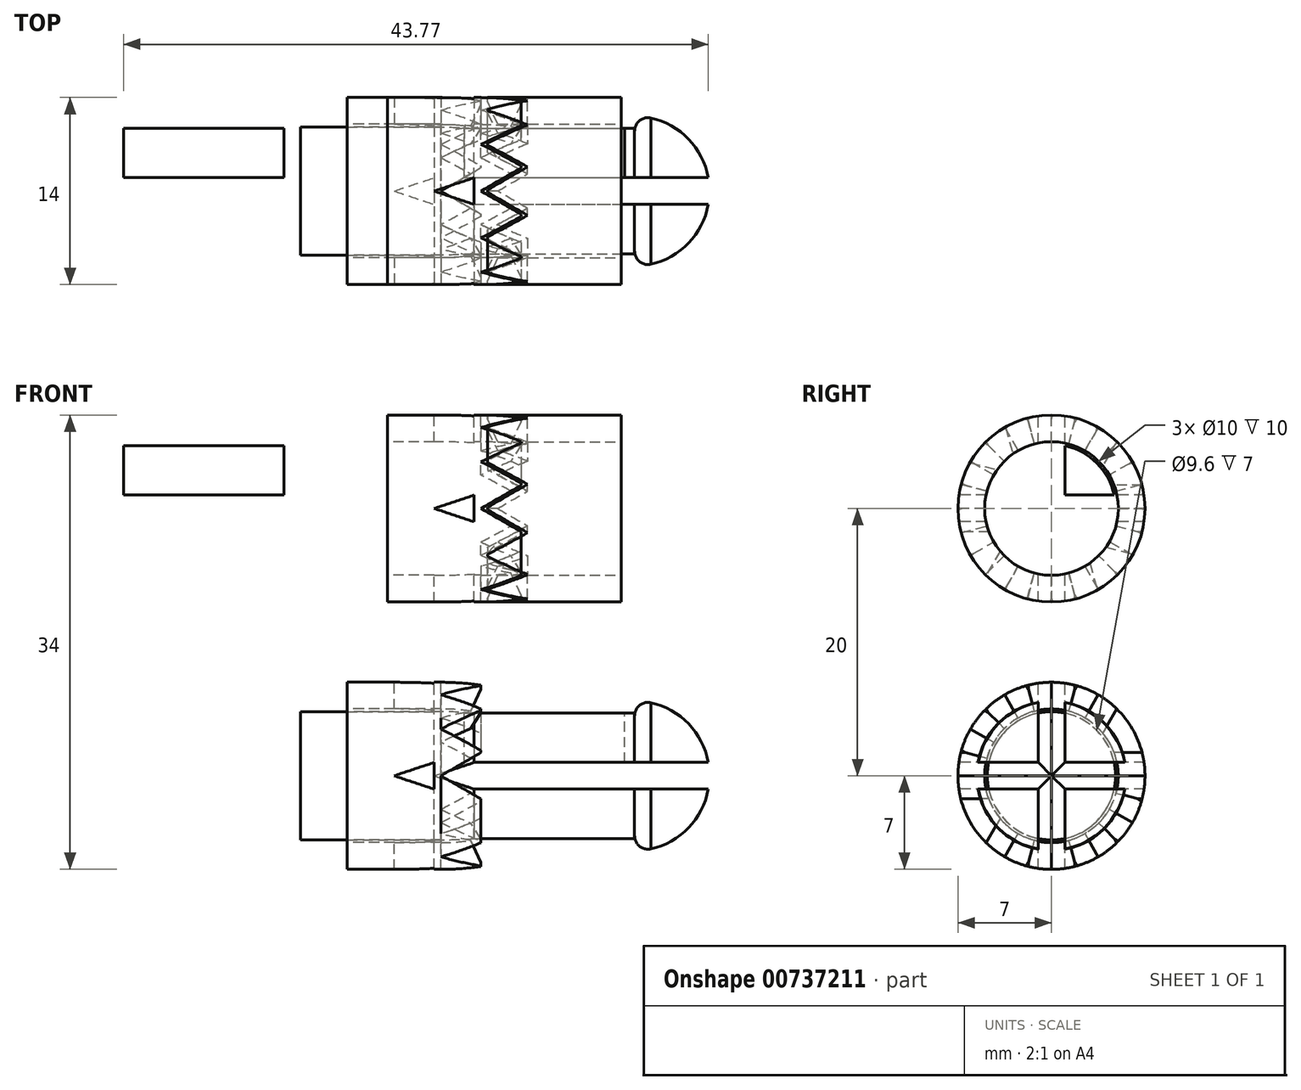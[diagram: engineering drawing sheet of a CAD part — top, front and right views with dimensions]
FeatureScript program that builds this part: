
annotation { "Feature Type Name" : "Feature", "Feature Type Description" : "" }
export const myFeature = defineFeature(function(context is Context, id is Id, definition is map)
    precondition{}
    {
        {
            var Q0;
            Q0=qCreatedBy(makeId("Right.planeOp"),FACE);
            var sketch = newSketch(context, id + "F0", { "sketchPlane" : qUnion([Q0])});
            skCircle(sketch, "E0", {"center": v(0, 0) * mm, "radius": 5 * mm});
            skCircle(sketch, "E1", {"center": v(0, 0) * mm, "radius": 7 * mm});
            skSolve(sketch);
        }
        {
            var Q0;
            Q0=makeQuery(id+"F0.imprint","IMPRINT",FACE,{"disambiguationData":[TD([[makeQuery(id+"F0.imprint","IMPRINT",EDGE,{"derivedFrom":sQuery(id+"F0.wireOp",EDGE,"E0")}),-1.0]])]});
            extrude(context, id + "F1", {"entities" : qUnion([Q0]), "oppositeDirection" : true, "depth" : 10 * mm, "offsetDistance" : 25 * mm});
        }
        {
            var Q0;
            Q0=makeQuery(id+"F1.opExtrude","CAP_FACE",FACE,{"disambiguationData":[OSD([sQuery(id+"F0.wireOp",EDGE,"E0"),sQuery(id+"F0.wireOp",EDGE,"E1")])],"isStart":false});
            var sketch = newSketch(context, id + "F2", { "sketchPlane" : qUnion([Q0])});
            skCircle(sketch, "E2.0", {"center": v(0, 0) * mm, "radius": 7 * mm});
            skCircle(sketch, "E3.cCircle", {"center": v(0, 0) * mm, "radius": 7 * mm, "construction": true});
            skLineSegment(sketch, "E3.0", {"start": v(-1.88, 7) * mm, "end": v(1.88, 7) * mm, "construction": true});
            skLineSegment(sketch, "E3.1", {"start": v(1.88, 7) * mm, "end": v(5.12, 5.12) * mm, "construction": true});
            skLineSegment(sketch, "E3.2", {"start": v(5.12, 5.12) * mm, "end": v(7, 1.88) * mm, "construction": true});
            skLineSegment(sketch, "E3.3", {"start": v(7, 1.88) * mm, "end": v(7, -1.88) * mm, "construction": true});
            skLineSegment(sketch, "E3.4", {"start": v(7, -1.88) * mm, "end": v(5.12, -5.12) * mm, "construction": true});
            skLineSegment(sketch, "E3.5", {"start": v(5.12, -5.12) * mm, "end": v(1.88, -7) * mm, "construction": true});
            skLineSegment(sketch, "E3.6", {"start": v(1.88, -7) * mm, "end": v(-1.88, -7) * mm, "construction": true});
            skLineSegment(sketch, "E3.7", {"start": v(-1.88, -7) * mm, "end": v(-5.12, -5.12) * mm, "construction": true});
            skLineSegment(sketch, "E3.8", {"start": v(-5.12, -5.12) * mm, "end": v(-7, -1.88) * mm, "construction": true});
            skLineSegment(sketch, "E3.9", {"start": v(-7, -1.88) * mm, "end": v(-7, 1.88) * mm, "construction": true});
            skLineSegment(sketch, "E3.10", {"start": v(-7, 1.88) * mm, "end": v(-5.12, 5.12) * mm, "construction": true});
            skLineSegment(sketch, "E3.11", {"start": v(-5.12, 5.12) * mm, "end": v(-1.88, 7) * mm, "construction": true});
            skPoint(sketch, "E3.0.midPoint", {"position": v(0, 7) * mm});
            skSolve(sketch);
        }
        {
            var Q0;
            Q0=sQuery(id+"F2.wireOp",EDGE,"E2.0");
            var Q1;
            Q1=sQuery(id+"F2.wireOp",VERTEX,"E3.3.start");
            cPlane(context, id + "F3", {"entities" : qUnion([Q0, Q1]), "cplaneType" : CPlaneType.CURVE_POINT, "offset" : 25 * mm, "width" : 150 * mm, "height" : 150 * mm});
        }
        {
            var Q0;
            Q0=qCreatedBy(id+"F3.planeOp",FACE);
            var sketch = newSketch(context, id + "F4", { "sketchPlane" : qUnion([Q0])});
            skLineSegment(sketch, "E4.0", {"start": v(-10, -7) * mm, "end": v(-10, 7) * mm});
            skLineSegment(sketch, "E4.1", {"start": v(0, 7) * mm, "end": v(0, -7) * mm});
            skLineSegment(sketch, "E5", {"start": v(0, 7) * mm, "end": v(-10, 7) * mm});
            skLineSegment(sketch, "E6", {"start": v(0, -7) * mm, "end": v(-10, -7) * mm});
            skLineSegment(sketch, "E7", {"start": v(-7, 7) * mm, "end": v(-7, -7) * mm});
            skPoint(sketch, "E8", {"position": v(-7, 0) * mm});
            skLineSegment(sketch, "E9", {"start": v(-7, 0) * mm, "end": v(-10, 1.73) * mm});
            skLineSegment(sketch, "E10", {"start": v(-7, 0) * mm, "end": v(-10, -1.73) * mm});
            skSolve(sketch);
        }
        {
            var Q0;
            Q0=sQuery(id+"F2.wireOp",EDGE,"E2.0");
            var Q1;
            Q1=sQuery(id+"F2.wireOp",VERTEX,"E3.2.start");
            cPlane(context, id + "F5", {"entities" : qUnion([Q0, Q1]), "cplaneType" : CPlaneType.CURVE_POINT, "offset" : 25 * mm, "width" : 150 * mm, "height" : 150 * mm});
        }
        {
            var Q0;
            Q0=qCreatedBy(id+"F5.planeOp",FACE);
            var sketch = newSketch(context, id + "F6", { "sketchPlane" : qUnion([Q0])});
            skLineSegment(sketch, "E11.0", {"start": v(10, 7) * mm, "end": v(10, -7) * mm});
            skLineSegment(sketch, "E12.0", {"start": v(0, -7) * mm, "end": v(0, 7) * mm});
            skLineSegment(sketch, "E13", {"start": v(0, -7) * mm, "end": v(10, -7) * mm});
            skLineSegment(sketch, "E14", {"start": v(0, 7) * mm, "end": v(10, 7) * mm});
            skLineSegment(sketch, "E15.0", {"start": v(7, -6.06) * mm, "end": v(7, 6.06) * mm});
            skLineSegment(sketch, "E16", {"start": v(7, 0) * mm, "end": v(10, -1.73) * mm});
            skLineSegment(sketch, "E17", {"start": v(7, 0) * mm, "end": v(10, 1.73) * mm});
            skSolve(sketch);
        }
        {
            var Q0;
            Q0=sQuery(id+"F2.wireOp",EDGE,"E2.0");
            var Q1;
            Q1=sQuery(id+"F2.wireOp",VERTEX,"E3.1.start");
            cPlane(context, id + "F7", {"entities" : qUnion([Q0, Q1]), "cplaneType" : CPlaneType.CURVE_POINT, "offset" : 25 * mm, "width" : 150 * mm, "height" : 150 * mm});
        }
        {
            var Q0;
            Q0=qCreatedBy(id+"F7.planeOp",FACE);
            var sketch = newSketch(context, id + "F8", { "sketchPlane" : qUnion([Q0])});
            skLineSegment(sketch, "E18.0", {"start": v(10, 7) * mm, "end": v(10, -7) * mm});
            skLineSegment(sketch, "E18.1", {"start": v(0, -7) * mm, "end": v(0, 7) * mm});
            skLineSegment(sketch, "E19", {"start": v(0, -7) * mm, "end": v(10, -7) * mm});
            skLineSegment(sketch, "E20", {"start": v(0, 7) * mm, "end": v(10, 7) * mm});
            skLineSegment(sketch, "E21.0", {"start": v(7, -5.25) * mm, "end": v(7, 5.25) * mm});
            skPoint(sketch, "E22", {"position": v(7, 0) * mm});
            skLineSegment(sketch, "E23", {"start": v(7, 0) * mm, "end": v(10, -1.73) * mm});
            skLineSegment(sketch, "E24", {"start": v(7, 0) * mm, "end": v(10, 1.73) * mm});
            skSolve(sketch);
        }
        {
            var Q0;
            Q0=sQuery(id+"F2.wireOp",EDGE,"E2.0");
            var Q1;
            Q1=sQuery(id+"F2.wireOp",VERTEX,"E3.11.end");
            cPlane(context, id + "F9", {"entities" : qUnion([Q0, Q1]), "cplaneType" : CPlaneType.CURVE_POINT, "offset" : 25 * mm, "width" : 150 * mm, "height" : 150 * mm});
        }
        {
            var Q0;
            Q0=qCreatedBy(id+"F9.planeOp",FACE);
            var sketch = newSketch(context, id + "F10", { "sketchPlane" : qUnion([Q0])});
            skLineSegment(sketch, "E25.0", {"start": v(10, 7) * mm, "end": v(10, -7) * mm});
            skLineSegment(sketch, "E25.1", {"start": v(0, -7) * mm, "end": v(0, 7) * mm});
            skLineSegment(sketch, "E26", {"start": v(0, -7) * mm, "end": v(10, -7) * mm});
            skLineSegment(sketch, "E27", {"start": v(0, 7) * mm, "end": v(10, 7) * mm});
            skLineSegment(sketch, "E28.0", {"start": v(7, -4.55) * mm, "end": v(7, 4.55) * mm});
            skPoint(sketch, "E29", {"position": v(7, 0) * mm});
            skLineSegment(sketch, "E30", {"start": v(7, 0) * mm, "end": v(10, 1.73) * mm});
            skLineSegment(sketch, "E31", {"start": v(7, 0) * mm, "end": v(10, -1.73) * mm});
            skSolve(sketch);
        }
        {
            var Q0;
            Q0=sQuery(id+"F2.wireOp",EDGE,"E2.0");
            var Q1;
            Q1=sQuery(id+"F2.wireOp",VERTEX,"E3.10.end");
            cPlane(context, id + "F11", {"entities" : qUnion([Q0, Q1]), "cplaneType" : CPlaneType.CURVE_POINT, "offset" : 25 * mm, "width" : 150 * mm, "height" : 150 * mm});
        }
        {
            var Q0;
            Q0=qCreatedBy(id+"F11.planeOp",FACE);
            var sketch = newSketch(context, id + "F12", { "sketchPlane" : qUnion([Q0])});
            skLineSegment(sketch, "E32.0", {"start": v(-10, -7) * mm, "end": v(-10, 7) * mm});
            skLineSegment(sketch, "E32.1", {"start": v(0, 7) * mm, "end": v(0, -7) * mm});
            skLineSegment(sketch, "E33", {"start": v(0, 7) * mm, "end": v(-10, 7) * mm});
            skLineSegment(sketch, "E34", {"start": v(0, -7) * mm, "end": v(-10, -7) * mm});
            skLineSegment(sketch, "E35.0", {"start": v(-7, 3.94) * mm, "end": v(-7, -3.94) * mm});
            skLineSegment(sketch, "E36", {"start": v(-7, 0) * mm, "end": v(-10, -1.73) * mm});
            skLineSegment(sketch, "E37", {"start": v(-7, 0) * mm, "end": v(-10, 1.73) * mm});
            skSolve(sketch);
        }
        {
            var Q0;
            Q0=sQuery(id+"F2.wireOp",EDGE,"E2.0");
            var Q1;
            Q1=sQuery(id+"F2.wireOp",VERTEX,"E3.9.end");
            cPlane(context, id + "F13", {"entities" : qUnion([Q0, Q1]), "cplaneType" : CPlaneType.CURVE_POINT, "offset" : 25 * mm, "width" : 150 * mm, "height" : 150 * mm});
        }
        {
            var Q0;
            Q0=qCreatedBy(id+"F13.planeOp",FACE);
            var sketch = newSketch(context, id + "F14", { "sketchPlane" : qUnion([Q0])});
            skLineSegment(sketch, "E38.0", {"start": v(-10, -7) * mm, "end": v(-10, 7) * mm});
            skLineSegment(sketch, "E38.1", {"start": v(0, 7) * mm, "end": v(0, -7) * mm});
            skLineSegment(sketch, "E39.0", {"start": v(-7, 3.4) * mm, "end": v(-7, -3.4) * mm});
            skLineSegment(sketch, "E40", {"start": v(-7, 0) * mm, "end": v(-10, 1.73) * mm});
            skLineSegment(sketch, "E41", {"start": v(-7, 0) * mm, "end": v(-10, -1.73) * mm});
            skSolve(sketch);
        }
        {
            var Q0;
            {var subQ0=sQuery(id+"F4.wireOp",EDGE,"E9");Q0=makeQuery(id+"F4.imprint","IMPRINT",FACE,{"disambiguationData":[TD([[makeQuery(id+"F4.imprint","IMPRINT",EDGE,{"derivedFrom":subQ0}),1.0]])]});}
            extrude(context, id + "F15", {"entities" : qUnion([Q0]), "operationType" : NewBodyOperationType.REMOVE, "endBound" : BoundingType.SYMMETRIC, "oppositeDirection" : true, "depth" : 14.5 * mm, "offsetDistance" : 25 * mm});
        }
        {
            var Q0;
            {var subQ0=sQuery(id+"F6.wireOp",EDGE,"E16");Q0=makeQuery(id+"F6.imprint","IMPRINT",FACE,{"disambiguationData":[TD([[makeQuery(id+"F6.imprint","IMPRINT",EDGE,{"derivedFrom":subQ0}),1.0]])]});}
            extrude(context, id + "F16", {"entities" : qUnion([Q0]), "operationType" : NewBodyOperationType.REMOVE, "endBound" : BoundingType.SYMMETRIC, "depth" : 14.5 * mm, "offsetDistance" : 25 * mm});
        }
        {
            var Q0;
            {var subQ0=sQuery(id+"F8.wireOp",EDGE,"E23");Q0=makeQuery(id+"F8.imprint","IMPRINT",FACE,{"disambiguationData":[TD([[makeQuery(id+"F8.imprint","IMPRINT",EDGE,{"derivedFrom":subQ0}),1.0]])]});}
            extrude(context, id + "F17", {"entities" : qUnion([Q0]), "operationType" : NewBodyOperationType.REMOVE, "endBound" : BoundingType.SYMMETRIC, "oppositeDirection" : true, "depth" : 14.5 * mm, "offsetDistance" : 25 * mm});
        }
        {
            var Q0;
            {var subQ0=sQuery(id+"F10.wireOp",EDGE,"E30");Q0=makeQuery(id+"F10.imprint","IMPRINT",FACE,{"disambiguationData":[TD([[makeQuery(id+"F10.imprint","IMPRINT",EDGE,{"derivedFrom":subQ0}),-1.0]])]});}
            extrude(context, id + "F18", {"entities" : qUnion([Q0]), "operationType" : NewBodyOperationType.REMOVE, "endBound" : BoundingType.SYMMETRIC, "oppositeDirection" : true, "depth" : 14.5 * mm, "offsetDistance" : 25 * mm});
        }
        {
            var Q0;
            {var subQ0=sQuery(id+"F14.wireOp",EDGE,"E40");Q0=makeQuery(id+"F14.imprint","IMPRINT",FACE,{"disambiguationData":[TD([[makeQuery(id+"F14.imprint","IMPRINT",EDGE,{"derivedFrom":subQ0}),1.0]])]});}
            extrude(context, id + "F19", {"entities" : qUnion([Q0]), "operationType" : NewBodyOperationType.REMOVE, "endBound" : BoundingType.SYMMETRIC, "oppositeDirection" : true, "depth" : 14.5 * mm, "offsetDistance" : 25 * mm});
        }
        {
            var Q0;
            {var subQ0=sQuery(id+"F12.wireOp",EDGE,"E36");Q0=makeQuery(id+"F12.imprint","IMPRINT",FACE,{"disambiguationData":[TD([[makeQuery(id+"F12.imprint","IMPRINT",EDGE,{"derivedFrom":subQ0}),-1.0]])]});}
            extrude(context, id + "F20", {"entities" : qUnion([Q0]), "operationType" : NewBodyOperationType.REMOVE, "endBound" : BoundingType.SYMMETRIC, "oppositeDirection" : true, "depth" : 14.5 * mm, "offsetDistance" : 25 * mm});
        }
        {
            var Q0;
            Q0=makeQuery(id+"F1.opExtrude","CAP_FACE",FACE,{"disambiguationData":[OSD([sQuery(id+"F0.wireOp",EDGE,"E0"),sQuery(id+"F0.wireOp",EDGE,"E1")])],"isStart":true});
            var sketch = newSketch(context, id + "F21", { "sketchPlane" : qUnion([Q0])});
            skCircle(sketch, "E42.0", {"center": v(0, 0) * mm, "radius": 7 * mm});
            skLineSegment(sketch, "E43", {"start": v(0, 7) * mm, "end": v(0, -7) * mm, "construction": true});
            skLineSegment(sketch, "E44", {"start": v(-7, 0) * mm, "end": v(7, 0) * mm, "construction": true});
            skSolve(sketch);
        }
        {
            var Q0;
            Q0=makeQuery(id+"F1.opExtrude","SWEPT_BODY",BODY,{"disambiguationData":[OSD([sQuery(id+"F0.wireOp",EDGE,"E0"),sQuery(id+"F0.wireOp",EDGE,"E1")])]});
            var Q1;
            Q1=sQuery(id+"F21.wireOp",EDGE,"E43");
            transform(context, id + "F22", {"entities" : qUnion([Q0]), "transformType" : TransformType.ROTATION, "transformAxis" : qUnion([Q1]), "angle" : 180 * degree, "makeCopy" : true});
        }
        {
            var Q0;
            Q0=makeQuery(id+"F22.opPattern","COPY",BODY,{"derivedFrom":makeQuery(id+"F1.opExtrude","SWEPT_BODY",BODY,{"disambiguationData":[OSD([sQuery(id+"F0.wireOp",EDGE,"E0"),sQuery(id+"F0.wireOp",EDGE,"E1")])]}),"instanceName":"1"});
            transform(context, id + "F23", {"entities" : qUnion([Q0]), "transformType" : TransformType.TRANSLATION_3D, "dx" : -17.5 * mm, "dy" : 0 * mm, "dz" : 0 * mm, "makeCopy" : false});
        }
        {
            var Q0;
            Q0=makeQuery(id+"F22.opPattern","COPY",BODY,{"derivedFrom":makeQuery(id+"F1.opExtrude","SWEPT_BODY",BODY,{"disambiguationData":[OSD([sQuery(id+"F0.wireOp",EDGE,"E0"),sQuery(id+"F0.wireOp",EDGE,"E1")])]}),"instanceName":"1"});
            var Q1;
            Q1=makeQuery(id+"F22.opPattern","COPY",EDGE,{"derivedFrom":makeQuery(id+"F1.opExtrude","CAP_EDGE",EDGE,{"disambiguationData":[OSD([sQuery(id+"F0.wireOp",EDGE,"E0")])],"isStart":true}),"instanceName":"1"});
            transform(context, id + "F24", {"entities" : qUnion([Q0]), "transformType" : TransformType.ROTATION, "transformAxis" : qUnion([Q1]), "angle" : 15 * degree, "makeCopy" : false});
        }
        {
            var Q0;
            Q0=makeQuery(id+"F1.opExtrude","CAP_FACE",FACE,{"disambiguationData":[OSD([sQuery(id+"F0.wireOp",EDGE,"E0"),sQuery(id+"F0.wireOp",EDGE,"E1")])],"isStart":true});
            cPlane(context, id + "F25", {"entities" : qUnion([Q0]), "cplaneType" : CPlaneType.OFFSET, "offset" : 1 * mm, "width" : 150 * mm, "height" : 150 * mm});
        }
        {
            var Q0;
            Q0=qCreatedBy(id+"F25.planeOp",FACE);
            var sketch = newSketch(context, id + "F26", { "sketchPlane" : qUnion([Q0])});
            skCircle(sketch, "E45", {"center": v(0, 0) * mm, "radius": 4.8 * mm});
            skLineSegment(sketch, "E46", {"start": v(0, 0) * mm, "end": v(4.8, 0) * mm});
            skLineSegment(sketch, "E47", {"start": v(0, 0) * mm, "end": v(-4.8, 0) * mm});
            skLineSegment(sketch, "E48", {"start": v(0, 0) * mm, "end": v(0, -4.8) * mm});
            skLineSegment(sketch, "E49", {"start": v(0, 0) * mm, "end": v(0, 4.8) * mm});
            skLineSegment(sketch, "E50.0", {"start": v(1, -1) * mm, "end": v(4.7, -1) * mm});
            skLineSegment(sketch, "E50.1", {"start": v(1, -1) * mm, "end": v(1, -4.7) * mm});
            skLineSegment(sketch, "E51.MirrorCS", {"start": v(1, 1) * mm, "end": v(4.7, 1) * mm});
            skLineSegment(sketch, "E52.MirrorCS", {"start": v(1, 1) * mm, "end": v(1, 4.7) * mm});
            skLineSegment(sketch, "E53.MirrorCS", {"start": v(-1, -1) * mm, "end": v(-1, -4.7) * mm});
            skLineSegment(sketch, "E54.MirrorCS", {"start": v(-1, -1) * mm, "end": v(-4.7, -1) * mm});
            skLineSegment(sketch, "E55.MirrorCS", {"start": v(-1, 1) * mm, "end": v(-4.7, 1) * mm});
            skLineSegment(sketch, "E56.MirrorCS", {"start": v(-1, 1) * mm, "end": v(-1, 4.7) * mm});
            skSolve(sketch);
        }
        {
            var Q0;
            {var subQ0=sQuery(id+"F26.wireOp",EDGE,"E51.MirrorCS");Q0=makeQuery(id+"F26.imprint","IMPRINT",FACE,{"disambiguationData":[TD([[makeQuery(id+"F26.imprint","IMPRINT",EDGE,{"derivedFrom":subQ0}),1.0]])]});}
            var Q1;
            {var subQ0=sQuery(id+"F26.wireOp",EDGE,"E50.0");Q1=makeQuery(id+"F26.imprint","IMPRINT",FACE,{"disambiguationData":[TD([[makeQuery(id+"F26.imprint","IMPRINT",EDGE,{"derivedFrom":subQ0}),-1.0]])]});}
            var Q2;
            {var subQ0=sQuery(id+"F26.wireOp",EDGE,"E53.MirrorCS");Q2=makeQuery(id+"F26.imprint","IMPRINT",FACE,{"disambiguationData":[TD([[makeQuery(id+"F26.imprint","IMPRINT",EDGE,{"derivedFrom":subQ0}),-1.0]])]});}
            var Q3;
            {var subQ0=sQuery(id+"F26.wireOp",EDGE,"E55.MirrorCS");Q3=makeQuery(id+"F26.imprint","IMPRINT",FACE,{"disambiguationData":[TD([[makeQuery(id+"F26.imprint","IMPRINT",EDGE,{"derivedFrom":subQ0}),-1.0]])]});}
            extrude(context, id + "F27", {"entities" : qUnion([Q0, Q1, Q2, Q3]), "oppositeDirection" : true, "depth" : 12 * mm, "offsetDistance" : 25 * mm});
        }
        {
            var Q0;
            Q0=makeQuery(id+"F27.opExtrude","CAP_FACE",FACE,{"disambiguationData":[OSD([sQuery(id+"F26.wireOp",EDGE,"E45"),sQuery(id+"F26.wireOp",EDGE,"E51.MirrorCS"),sQuery(id+"F26.wireOp",EDGE,"E52.MirrorCS")])],"isStart":false});
            var sketch = newSketch(context, id + "F28", { "sketchPlane" : qUnion([Q0])});
            skPoint(sketch, "E57.0", {"position": v(0, 0) * mm});
            skLineSegment(sketch, "E58.0", {"start": v(1, 1) * mm, "end": v(1, 4.7) * mm});
            skLineSegment(sketch, "E58.1", {"start": v(1, 1) * mm, "end": v(4.7, 1) * mm});
            skArc(sketch, "E58.2", {"start": v(1, 4.7) * mm, "mid": v(3.4, 3.4) * mm, "end": v(4.7, 1) * mm});
            skLineSegment(sketch, "E58.3", {"start": v(-1, 1) * mm, "end": v(-1, 4.7) * mm});
            skArc(sketch, "E58.4", {"start": v(-4.7, 1) * mm, "mid": v(-3.4, 3.4) * mm, "end": v(-1, 4.7) * mm});
            skLineSegment(sketch, "E58.5", {"start": v(-1, 1) * mm, "end": v(-4.7, 1) * mm});
            skLineSegment(sketch, "E58.6", {"start": v(-1, -1) * mm, "end": v(-4.7, -1) * mm});
            skLineSegment(sketch, "E58.7", {"start": v(-1, -1) * mm, "end": v(-1, -4.7) * mm});
            skLineSegment(sketch, "E58.8", {"start": v(1, -1) * mm, "end": v(1, -4.7) * mm});
            skLineSegment(sketch, "E58.9", {"start": v(1, -1) * mm, "end": v(4.7, -1) * mm});
            skArc(sketch, "E58.10", {"start": v(4.7, -1) * mm, "mid": v(3.4, -3.4) * mm, "end": v(1, -4.7) * mm});
            skArc(sketch, "E58.11", {"start": v(-1, -4.7) * mm, "mid": v(-3.4, -3.4) * mm, "end": v(-4.7, -1) * mm});
            skCircle(sketch, "E59", {"center": v(0, 0) * mm, "radius": 4.8 * mm});
            skSolve(sketch);
        }
        {
            var Q0;
            {var subQ2=sQuery(id+"F28.wireOp",EDGE,"E58.0");Q0=makeQuery(id+"F28.imprint","IMPRINT",FACE,{"disambiguationData":[TD([[makeQuery(id+"F28.imprint","IMPRINT",EDGE,{"derivedFrom":subQ2}),1.0]])]});}
            var Q1;
            {var subQ0=sQuery(id+"F28.wireOp",EDGE,"E58.3");Q1=makeQuery(id+"F28.imprint","IMPRINT",FACE,{"disambiguationData":[TD([[makeQuery(id+"F28.imprint","IMPRINT",EDGE,{"derivedFrom":subQ0}),1.0]])]});}
            var Q2;
            {var subQ0=sQuery(id+"F28.wireOp",EDGE,"E58.6");Q2=makeQuery(id+"F28.imprint","IMPRINT",FACE,{"disambiguationData":[TD([[makeQuery(id+"F28.imprint","IMPRINT",EDGE,{"derivedFrom":subQ0}),1.0]])]});}
            var Q3;
            {var subQ0=sQuery(id+"F28.wireOp",EDGE,"E58.0");Q3=makeQuery(id+"F28.imprint","IMPRINT",FACE,{"disambiguationData":[TD([[makeQuery(id+"F28.imprint","IMPRINT",EDGE,{"derivedFrom":subQ0}),-1.0]])]});}
            var Q4;
            {var subQ0=sQuery(id+"F28.wireOp",EDGE,"E58.8");Q4=makeQuery(id+"F28.imprint","IMPRINT",FACE,{"disambiguationData":[TD([[makeQuery(id+"F28.imprint","IMPRINT",EDGE,{"derivedFrom":subQ0}),1.0]])]});}
            extrude(context, id + "F29", {"entities" : qUnion([Q0, Q1, Q2, Q3, Q4]), "depth" : 15 * mm, "offsetDistance" : 25 * mm});
        }
        {
            var Q0;
            Q0=qCreatedBy(makeId("Front.planeOp"),FACE);
            var sketch = newSketch(context, id + "F30", { "sketchPlane" : qUnion([Q0])});
            skLineSegment(sketch, "E60.0", {"start": v(-11, -4.8) * mm, "end": v(-11, 4.8) * mm});
            skLineSegment(sketch, "E61", {"start": v(-11, 4.8) * mm, "end": v(-14, 4.8) * mm});
            skLineSegment(sketch, "E62", {"start": v(-14, 4.8) * mm, "end": v(-14, -4.8) * mm});
            skLineSegment(sketch, "E63", {"start": v(-14, -4.8) * mm, "end": v(-11, -4.8) * mm});
            skPoint(sketch, "E64", {"position": v(-14, 0) * mm});
            skLineSegment(sketch, "E65.0", {"start": v(-11, 1) * mm, "end": v(1, 1) * mm});
            skLineSegment(sketch, "E65.1", {"start": v(-11, -1) * mm, "end": v(1, -1) * mm});
            skLineSegment(sketch, "E66", {"start": v(-14, 0) * mm, "end": v(-11, 1) * mm});
            skLineSegment(sketch, "E67", {"start": v(-14, 0) * mm, "end": v(-11, -1) * mm});
            skSolve(sketch);
        }
        {
            var Q0;
            {var subQ0=sQuery(id+"F30.wireOp",EDGE,"E66");Q0=makeQuery(id+"F30.imprint","IMPRINT",FACE,{"disambiguationData":[TD([[makeQuery(id+"F30.imprint","IMPRINT",EDGE,{"derivedFrom":subQ0}),-1.0]])]});}
            extrude(context, id + "F31", {"entities" : qUnion([Q0]), "operationType" : NewBodyOperationType.REMOVE, "endBound" : BoundingType.SYMMETRIC, "oppositeDirection" : true, "depth" : 14.5 * mm, "offsetDistance" : 25 * mm});
        }
        {
            var Q0;
            Q0=qCreatedBy(makeId("Top.planeOp"),FACE);
            var sketch = newSketch(context, id + "F32", { "sketchPlane" : qUnion([Q0])});
            skLineSegment(sketch, "E68.0", {"start": v(-11, 4.7) * mm, "end": v(-11, -4.7) * mm});
            skLineSegment(sketch, "E68.1", {"start": v(-11, -1) * mm, "end": v(1, -1) * mm});
            skLineSegment(sketch, "E68.2", {"start": v(-11, 1) * mm, "end": v(1, 1) * mm});
            skLineSegment(sketch, "E69", {"start": v(-11, -4.7) * mm, "end": v(-14, -4.7) * mm});
            skLineSegment(sketch, "E70", {"start": v(-14, -4.7) * mm, "end": v(-14, 4.7) * mm});
            skLineSegment(sketch, "E71", {"start": v(-14, 4.7) * mm, "end": v(-11, 4.7) * mm});
            skPoint(sketch, "E72", {"position": v(-14, 0) * mm});
            skLineSegment(sketch, "E73", {"start": v(-14, 0) * mm, "end": v(-11, -1) * mm});
            skLineSegment(sketch, "E74", {"start": v(-14, 0) * mm, "end": v(-11, 1) * mm});
            skSolve(sketch);
        }
        {
            var Q0;
            {var subQ0=sQuery(id+"F32.wireOp",EDGE,"E73");Q0=makeQuery(id+"F32.imprint","IMPRINT",FACE,{"disambiguationData":[TD([[makeQuery(id+"F32.imprint","IMPRINT",EDGE,{"derivedFrom":subQ0}),1.0]])]});}
            extrude(context, id + "F33", {"entities" : qUnion([Q0]), "operationType" : NewBodyOperationType.REMOVE, "endBound" : BoundingType.SYMMETRIC, "oppositeDirection" : true, "depth" : 14.5 * mm, "offsetDistance" : 25 * mm});
        }
        {
            var Q0;
            Q0=qCreatedBy(id+"F25.planeOp",FACE);
            var sketch = newSketch(context, id + "F34", { "sketchPlane" : qUnion([Q0])});
            skLineSegment(sketch, "E75.0", {"start": v(0, 0) * mm, "end": v(-4.8, 0) * mm});
            skLineSegment(sketch, "E75.1", {"start": v(4.8, 0) * mm, "end": v(0, 0) * mm});
            skLineSegment(sketch, "E75.2", {"start": v(0, 0) * mm, "end": v(0, 4.8) * mm});
            skLineSegment(sketch, "E75.3", {"start": v(0, -4.8) * mm, "end": v(0, 0) * mm});
            skLineSegment(sketch, "E76.0", {"start": v(-1, 1) * mm, "end": v(-4.7, 1) * mm});
            skLineSegment(sketch, "E76.1", {"start": v(-1, -1) * mm, "end": v(-4.7, -1) * mm});
            skLineSegment(sketch, "E76.2", {"start": v(-1, -1) * mm, "end": v(-1, -4.7) * mm});
            skLineSegment(sketch, "E76.3", {"start": v(1, -1) * mm, "end": v(1, -4.7) * mm});
            skLineSegment(sketch, "E76.4", {"start": v(1, 1) * mm, "end": v(1, 4.7) * mm});
            skLineSegment(sketch, "E76.5", {"start": v(-1, 1) * mm, "end": v(-1, 4.7) * mm});
            skLineSegment(sketch, "E76.6", {"start": v(1, -1) * mm, "end": v(4.7, -1) * mm});
            skLineSegment(sketch, "E76.7", {"start": v(1, 1) * mm, "end": v(4.7, 1) * mm});
            skLineSegment(sketch, "E77", {"start": v(-4.7, -1) * mm, "end": v(-5.7, -1) * mm});
            skLineSegment(sketch, "E78", {"start": v(-5.7, -1) * mm, "end": v(-5.7, 1) * mm});
            skLineSegment(sketch, "E79", {"start": v(-5.7, 1) * mm, "end": v(-4.7, 1) * mm});
            skLineSegment(sketch, "E80", {"start": v(-1, -4.7) * mm, "end": v(-1, -5.7) * mm});
            skLineSegment(sketch, "E81", {"start": v(-1, -5.7) * mm, "end": v(1, -5.7) * mm});
            skLineSegment(sketch, "E82", {"start": v(1, -5.7) * mm, "end": v(1, -4.7) * mm});
            skLineSegment(sketch, "E83", {"start": v(4.7, -1) * mm, "end": v(5.7, -1) * mm});
            skLineSegment(sketch, "E84", {"start": v(5.7, -1) * mm, "end": v(5.7, 1) * mm});
            skLineSegment(sketch, "E85", {"start": v(5.7, 1) * mm, "end": v(4.7, 1) * mm});
            skLineSegment(sketch, "E86", {"start": v(1, 4.7) * mm, "end": v(1, 5.7) * mm});
            skLineSegment(sketch, "E87", {"start": v(1, 5.7) * mm, "end": v(-1, 5.7) * mm});
            skLineSegment(sketch, "E88", {"start": v(-1, 5.7) * mm, "end": v(-1, 4.7) * mm});
            skCircle(sketch, "E89", {"center": v(0, 0) * mm, "radius": 5.7 * mm});
            skLineSegment(sketch, "E90", {"start": v(4.8, 0) * mm, "end": v(5.7, 0) * mm});
            skLineSegment(sketch, "E91", {"start": v(0, 4.8) * mm, "end": v(0, 5.7) * mm});
            skLineSegment(sketch, "E92", {"start": v(-4.8, 0) * mm, "end": v(-5.7, 0) * mm});
            skLineSegment(sketch, "E93", {"start": v(0, -4.8) * mm, "end": v(0, -5.7) * mm});
            skSolve(sketch);
        }
        {
            var Q0;
            {var subQ3=sQuery(id+"F34.wireOp",EDGE,"E75.0");Q0=makeQuery(id+"F34.imprint","IMPRINT",FACE,{"disambiguationData":[TD([[makeQuery(id+"F34.imprint","IMPRINT",EDGE,{"derivedFrom":subQ3}),1.0]])]});}
            var Q1;
            {var subQ3=sQuery(id+"F34.wireOp",EDGE,"E75.0");Q1=makeQuery(id+"F34.imprint","IMPRINT",FACE,{"disambiguationData":[TD([[makeQuery(id+"F34.imprint","IMPRINT",EDGE,{"derivedFrom":subQ3}),-1.0]])]});}
            var Q2;
            {var subQ0=sQuery(id+"F34.wireOp",EDGE,"E76.0");Q2=makeQuery(id+"F34.imprint","IMPRINT",FACE,{"disambiguationData":[TD([[makeQuery(id+"F34.imprint","IMPRINT",EDGE,{"derivedFrom":subQ0}),-1.0]])]});}
            var Q3;
            {var subQ0=sQuery(id+"F34.wireOp",EDGE,"E76.1");Q3=makeQuery(id+"F34.imprint","IMPRINT",FACE,{"disambiguationData":[TD([[makeQuery(id+"F34.imprint","IMPRINT",EDGE,{"derivedFrom":subQ0}),1.0]])]});}
            var Q4;
            Q4=sQuery(id+"F34.wireOp",EDGE,"E75.2");
            revolve(context, id + "F35", {"surfaceOperationType" : NewSurfaceOperationType.NEW, "entities" : qUnion([Q0, Q1, Q2, Q3]), "axis" : qUnion([Q4]), "revolveType" : RevolveType.ONE_DIRECTION, "angle" : 180 * degree});
        }
        {
            var Q0;
            {var subQ3=sQuery(id+"F34.wireOp",EDGE,"E75.0");Q0=makeQuery(id+"F34.imprint","IMPRINT",FACE,{"disambiguationData":[TD([[makeQuery(id+"F34.imprint","IMPRINT",EDGE,{"derivedFrom":subQ3}),1.0]])]});}
            var Q1;
            {var subQ3=sQuery(id+"F34.wireOp",EDGE,"E75.0");Q1=makeQuery(id+"F34.imprint","IMPRINT",FACE,{"disambiguationData":[TD([[makeQuery(id+"F34.imprint","IMPRINT",EDGE,{"derivedFrom":subQ3}),-1.0]])]});}
            var Q2;
            {var subQ0=sQuery(id+"F34.wireOp",EDGE,"E77");Q2=makeQuery(id+"F34.imprint","IMPRINT",FACE,{"disambiguationData":[TD([[makeQuery(id+"F34.imprint","IMPRINT",EDGE,{"derivedFrom":subQ0}),-1.0]])]});}
            var Q3;
            {var subQ1=sQuery(id+"F34.wireOp",EDGE,"E75.2");Q3=makeQuery(id+"F34.imprint","IMPRINT",FACE,{"disambiguationData":[TD([[makeQuery(id+"F34.imprint","IMPRINT",EDGE,{"derivedFrom":subQ1}),-1.0]])]});}
            var Q4;
            Q4=makeQuery(id+"F34.imprint","IMPRINT",FACE,{"disambiguationData":[TD([[makeQuery(id+"F34.imprint","IMPRINT",EDGE,{"derivedFrom":sQuery(id+"F34.wireOp",EDGE,"E75.1")}),1.0]])]});
            extrude(context, id + "F36", {"entities" : qUnion([Q0, Q1, Q2, Q3, Q4]), "operationType" : NewBodyOperationType.REMOVE, "endBound" : BoundingType.THROUGH_ALL, "depth" : 25 * mm, "offsetDistance" : 25 * mm});
        }
        {
            var Q0;
            Q0=makeQuery(id+"F29.opExtrude","CAP_FACE",FACE,{"disambiguationData":[OSD([sQuery(id+"F28.wireOp",EDGE,"E59")])],"isStart":false});
            extrude(context, id + "F37", {"entities" : qUnion([Q0]), "operationType" : NewBodyOperationType.REMOVE, "oppositeDirection" : true, "depth" : 2 * mm, "offsetDistance" : 25 * mm});
        }
        {
            var Q0;
            {var subQ0=sQuery(id+"F34.wireOp",EDGE,"E89");Q0=makeQuery(id+"F36.boolean.opBoolean","SPLIT",EDGE,{"disambiguationData":[TD([makeQuery(id+"F36.opExtrude","SWEPT_FACE",FACE,{"disambiguationData":[OSD([sQuery(id+"F34.wireOp",EDGE,"E76.4"),sQuery(id+"F34.wireOp",EDGE,"E86")])]})])],"derivedFrom":makeQuery(id+"F35.opRevolve","CAP_EDGE",EDGE,{"disambiguationData":[OSD([subQ0])],"isStart":false})});}
            var Q1;
            {var subQ0=sQuery(id+"F34.wireOp",EDGE,"E89");Q1=makeQuery(id+"F36.boolean.opBoolean","SPLIT",EDGE,{"disambiguationData":[TD([makeQuery(id+"F36.opExtrude","SWEPT_FACE",FACE,{"disambiguationData":[OSD([sQuery(id+"F34.wireOp",EDGE,"E76.3"),sQuery(id+"F34.wireOp",EDGE,"E82")])]})])],"derivedFrom":makeQuery(id+"F35.opRevolve","CAP_EDGE",EDGE,{"disambiguationData":[OSD([subQ0])],"isStart":false})});}
            var Q2;
            {var subQ0=sQuery(id+"F34.wireOp",EDGE,"E89");Q2=makeQuery(id+"F36.boolean.opBoolean","SPLIT",EDGE,{"disambiguationData":[TD([makeQuery(id+"F36.opExtrude","SWEPT_FACE",FACE,{"disambiguationData":[OSD([sQuery(id+"F34.wireOp",EDGE,"E76.1"),sQuery(id+"F34.wireOp",EDGE,"E77")])]})])],"derivedFrom":makeQuery(id+"F35.opRevolve","CAP_EDGE",EDGE,{"disambiguationData":[OSD([subQ0])],"isStart":false})});}
            var Q3;
            {var subQ0=sQuery(id+"F34.wireOp",EDGE,"E89");Q3=makeQuery(id+"F36.boolean.opBoolean","SPLIT",EDGE,{"disambiguationData":[TD([makeQuery(id+"F36.opExtrude","SWEPT_FACE",FACE,{"disambiguationData":[OSD([sQuery(id+"F34.wireOp",EDGE,"E76.0"),sQuery(id+"F34.wireOp",EDGE,"E79")])]})])],"derivedFrom":makeQuery(id+"F35.opRevolve","CAP_EDGE",EDGE,{"disambiguationData":[OSD([subQ0])],"isStart":false})});}
            fillet(context, id + "F38", {"entities" : qUnion([Q0, Q1, Q2, Q3]), "radius" : 1 * mm, "tangentPropagation" : true, "allowEdgeOverflow" : false});
        }
        {
            var Q0;
            Q0=makeQuery(id+"F27.opExtrude","SWEPT_BODY",BODY,{"disambiguationData":[OSD([sQuery(id+"F26.wireOp",EDGE,"E45"),sQuery(id+"F26.wireOp",EDGE,"E51.MirrorCS"),sQuery(id+"F26.wireOp",EDGE,"E52.MirrorCS")])]});
            transform(context, id + "F39", {"entities" : qUnion([Q0]), "transformType" : TransformType.TRANSLATION_3D, "dx" : -.75 * mm, "dy" : 0 * mm, "dz" : 0 * mm, "makeCopy" : false});
        }
        {
            var Q0;
            Q0=makeQuery(id+"F1.opExtrude","SWEPT_BODY",BODY,{"disambiguationData":[OSD([sQuery(id+"F0.wireOp",EDGE,"E0"),sQuery(id+"F0.wireOp",EDGE,"E1")])]});
            transform(context, id + "F40", {"entities" : qUnion([Q0]), "transformType" : TransformType.TRANSLATION_3D, "dx" : 0 * mm, "dy" : 0 * mm, "dz" : 20 * mm, "makeCopy" : true});
        }
        {
            var Q0;
            Q0=makeQuery(id+"F22.opPattern","COPY",BODY,{"derivedFrom":makeQuery(id+"F1.opExtrude","SWEPT_BODY",BODY,{"disambiguationData":[OSD([sQuery(id+"F0.wireOp",EDGE,"E0"),sQuery(id+"F0.wireOp",EDGE,"E1")])]}),"instanceName":"1"});
            transform(context, id + "F41", {"entities" : qUnion([Q0]), "transformType" : TransformType.TRANSLATION_3D, "dx" : 0 * mm, "dy" : 0 * mm, "dz" : 20 * mm, "makeCopy" : true});
        }
        {
            var Q0;
            Q0=makeQuery(id+"F1.opExtrude","SWEPT_BODY",BODY,{"disambiguationData":[OSD([sQuery(id+"F0.wireOp",EDGE,"E0"),sQuery(id+"F0.wireOp",EDGE,"E1")])]});
            deleteBodies(context, id + "F42", {"entities" : qUnion([Q0])});
        }
        {
            var Q0;
            Q0=makeQuery(id+"F27.opExtrude","SWEPT_BODY",BODY,{"disambiguationData":[OSD([sQuery(id+"F26.wireOp",EDGE,"E45"),sQuery(id+"F26.wireOp",EDGE,"E51.MirrorCS"),sQuery(id+"F26.wireOp",EDGE,"E52.MirrorCS")])]});
            transform(context, id + "F43", {"entities" : qUnion([Q0]), "transformType" : TransformType.TRANSLATION_3D, "dx" : -25.5 * mm, "dy" : 0 * mm, "dz" : 20 * mm, "makeCopy" : true});
        }
        {
            var Q0;
            Q0=makeQuery(id+"F22.opPattern","COPY",BODY,{"derivedFrom":makeQuery(id+"F1.opExtrude","SWEPT_BODY",BODY,{"disambiguationData":[OSD([sQuery(id+"F0.wireOp",EDGE,"E0"),sQuery(id+"F0.wireOp",EDGE,"E1")])]}),"instanceName":"1"});
            transform(context, id + "F44", {"entities" : qUnion([Q0]), "transformType" : TransformType.TRANSLATION_3D, "dx" : -3 * mm, "dy" : 0 * mm, "dz" : 0 * mm, "makeCopy" : false});
        }
        {
            var Q0;
            Q0=makeQuery(id+"F22.opPattern","COPY",FACE,{"derivedFrom":makeQuery(id+"F1.opExtrude","CAP_FACE",FACE,{"disambiguationData":[OSD([sQuery(id+"F0.wireOp",EDGE,"E0"),sQuery(id+"F0.wireOp",EDGE,"E1")])],"isStart":true}),"instanceName":"1"});
            var sketch = newSketch(context, id + "F45", { "sketchPlane" : qUnion([Q0])});
            skCircle(sketch, "E94.0", {"center": v(0, 0) * mm, "radius": 5 * mm});
            skCircle(sketch, "E94.1", {"center": v(0, 0) * mm, "radius": 4.8 * mm});
            skSolve(sketch);
        }
        {
            var Q0;
            Q0=makeQuery(id+"F45.imprint","IMPRINT",FACE,{"disambiguationData":[TD([[makeQuery(id+"F45.imprint","IMPRINT",EDGE,{"derivedFrom":sQuery(id+"F45.wireOp",EDGE,"E94.0")}),1.0]])]});
            extrude(context, id + "F46", {"entities" : qUnion([Q0]), "oppositeDirection" : true, "depth" : 7 * mm, "offsetDistance" : 25 * mm});
        }
    });
